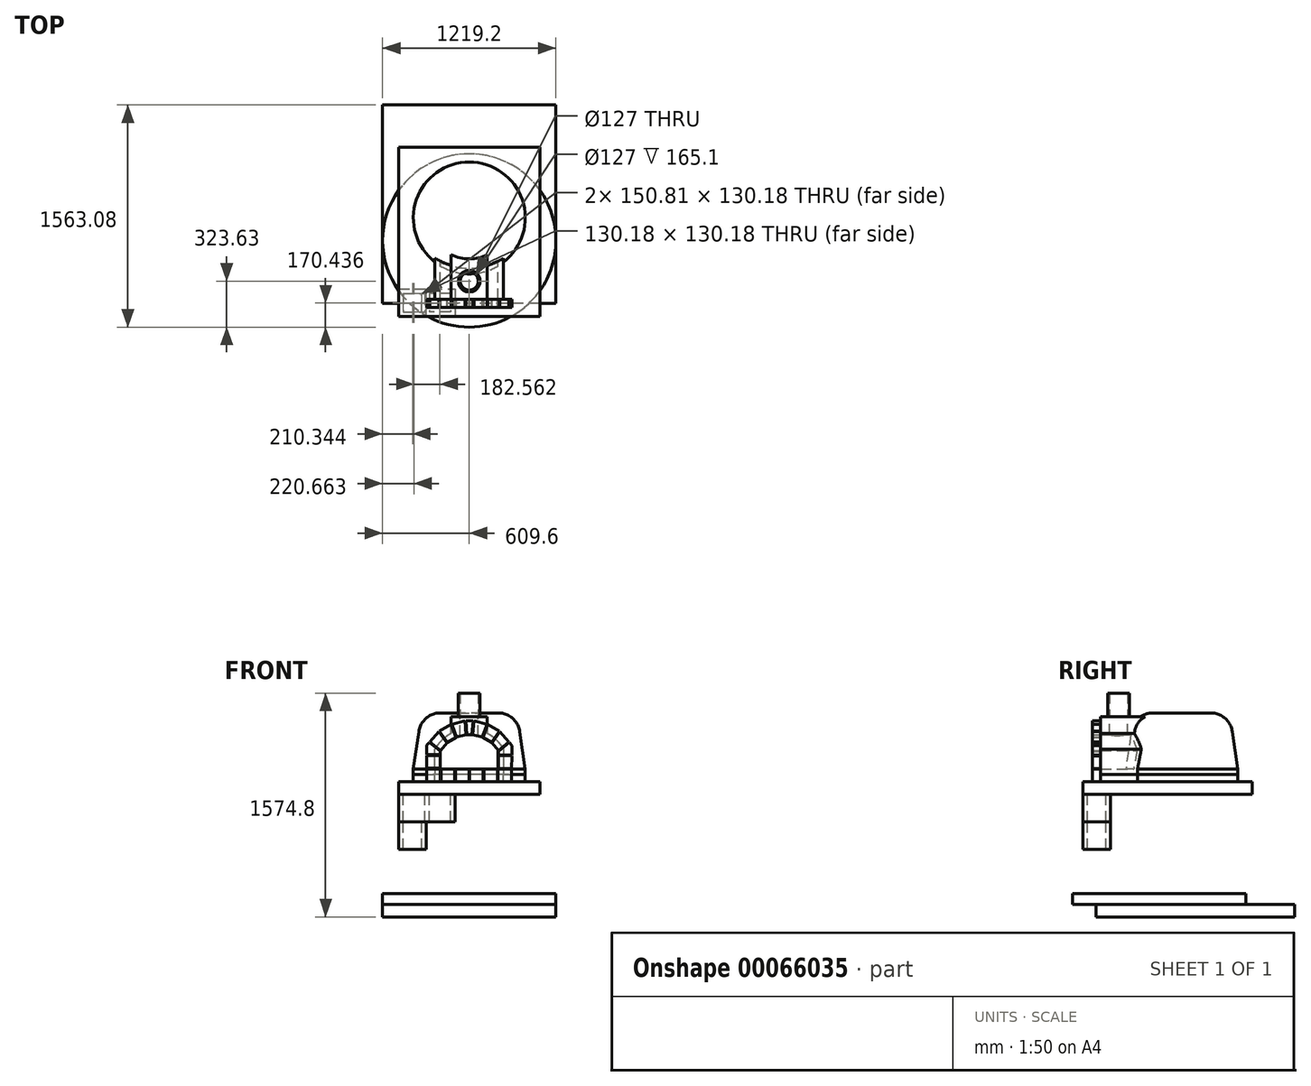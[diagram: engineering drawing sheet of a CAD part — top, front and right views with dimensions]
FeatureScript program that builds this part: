
annotation { "Feature Type Name" : "Feature", "Feature Type Description" : "" }
export const myFeature = defineFeature(function(context is Context, id is Id, definition is map)
    precondition{}
    {
        {
            var Q0;
            Q0=qCreatedBy(makeId("Top.planeOp"),FACE);
            var sketch = newSketch(context, id + "F0", { "sketchPlane" : qUnion([Q0])});
            skCircle(sketch, "E0", {"center": v(0, 0) * mm, "radius": 393.7 * mm});
            skSolve(sketch);
        }
        {
            var Q0;
            Q0=makeQuery(id+"F0.imprint","IMPRINT",FACE,{"disambiguationData":[TD([[makeQuery(id+"F0.imprint","IMPRINT",EDGE,{"derivedFrom":sQuery(id+"F0.wireOp",EDGE,"E0")}),1.0]])]});
            extrude(context, id + "F1", {"entities" : qUnion([Q0]), "depth" : 38.1 * mm});
        }
        {
            var Q0;
            Q0=makeQuery(id+"F1.opExtrude","CAP_FACE",FACE,{"disambiguationData":[OSD([sQuery(id+"F0.wireOp",EDGE,"E0")])],"isStart":false});
            extrude(context, id + "F2", {"entities" : qUnion([Q0]), "operationType" : NewBodyOperationType.ADD, "depth" : 393.7 * mm, "hasDraft" : true, "draftAngle" : 8.4 * degree, "draftPullDirection" : true});
        }
        {
            var Q0;
            Q0=makeQuery(id+"F2.opExtrude","CAP_EDGE",EDGE,{"disambiguationData":[OSD([sQuery(id+"F0.wireOp",EDGE,"E0")])],"isStart":false});
            fillet(context, id + "F3", {"entities" : qUnion([Q0]), "radius" : 152.4 * mm, "tangentPropagation" : true, "allowEdgeOverflow" : false});
        }
        {
            var Q0;
            Q0=qCreatedBy(makeId("Front.planeOp"),FACE);
            var sketch = newSketch(context, id + "F4", { "sketchPlane" : qUnion([Q0])});
            skLineSegment(sketch, "E1", {"start": v(0, 0) * mm, "end": v(-241.3, 0) * mm});
            skLineSegment(sketch, "E2", {"start": v(-241.3, 0) * mm, "end": v(-241.3, 177.8) * mm});
            skLineSegment(sketch, "E3", {"start": v(241.3, 177.8) * mm, "end": v(241.3, 0) * mm});
            skLineSegment(sketch, "E4", {"start": v(241.3, 0) * mm, "end": v(0, 0) * mm});
            skLineSegment(sketch, "E5", {"start": v(-203.2, 167.24) * mm, "end": v(-203.2, 38.1) * mm});
            skLineSegment(sketch, "E6", {"start": v(-203.2, 38.1) * mm, "end": v(203.2, 38.1) * mm});
            skLineSegment(sketch, "E7", {"start": v(203.2, 38.1) * mm, "end": v(203.2, 167.24) * mm});
            skLineSegment(sketch, "E8", {"start": v(0, 279.4) * mm, "end": v(0, 38.1) * mm, "construction": true});
            skLineSegment(sketch, "E9", {"start": v(0, 279.4) * mm, "end": v(0, 317.5) * mm, "construction": true});
            skArc(sketch, "E10", {"start": v(241.3, 177.8) * mm, "mid": v(0, 317.5) * mm, "end": v(-241.3, 177.8) * mm});
            skArc(sketch, "E11.0", {"start": v(203.2, 167.24) * mm, "mid": v(0, 279.4) * mm, "end": v(-203.2, 167.24) * mm});
            skSolve(sketch);
        }
        {
            var Q0;
            Q0 = qSketchRegion(id + "F4", true);
            extrude(context, id + "F5", {"entities" : qUnion([Q0]), "operationType" : NewBodyOperationType.ADD, "depth" : 571.5 * mm});
        }
        {
            var Q0;
            Q0=makeQuery(id+"F5.opExtrude","CAP_FACE",FACE,{"disambiguationData":[OSD([sQuery(id+"F4.wireOp",EDGE,"E1"),sQuery(id+"F4.wireOp",EDGE,"E2"),sQuery(id+"F4.wireOp",EDGE,"E3"),sQuery(id+"F4.wireOp",EDGE,"E4"),sQuery(id+"F4.wireOp",EDGE,"12a89784-33c5-42e5-a8f3-46ffcfec6846"),sQuery(id+"F4.wireOp",EDGE,"6c7c6252-bcdf-4629-810e-ab4d8ebfa29d.0"),sQuery(id+"F4.wireOp",EDGE,"Gnud8bc5-uh5z-W3xU-uaeR-RgDmJmBSCtFp")])],"isStart":false});
            var sketch = newSketch(context, id + "F6", { "sketchPlane" : qUnion([Q0])});
            skLineSegment(sketch, "E12", {"start": v(0, 406.4) * mm, "end": v(-127, 406.4) * mm});
            skPoint(sketch, "E12.startSnap0", {"position": v(0, 304.48) * mm});
            skLineSegment(sketch, "E13", {"start": v(-127, 406.4) * mm, "end": v(-127, 272.25) * mm});
            skLineSegment(sketch, "E14", {"start": v(0, 406.4) * mm, "end": v(127, 406.4) * mm});
            skLineSegment(sketch, "E15", {"start": v(127, 406.4) * mm, "end": v(127, 272.25) * mm});
            skArc(sketch, "E16", {"start": v(127, 272.25) * mm, "mid": v(0, 304.48) * mm, "end": v(-127, 272.25) * mm});
            skSolve(sketch);
        }
        {
            var Q0;
            Q0 = qSketchRegion(id + "F6", true);
            var Q1;
            Q1=makeQuery(id+"F3.opFillet","BLEND_FACE",FACE,{"disambiguationData":[OSD([sQuery(id+"F0.wireOp",EDGE,"E0")])]});
            extrude(context, id + "F7", {"entities" : qUnion([Q0]), "operationType" : NewBodyOperationType.ADD, "endBound" : BoundingType.UP_TO_SURFACE, "oppositeDirection" : true, "endBoundEntityFace" : qUnion([Q1]), "depth" : 355.6 * mm});
        }
        {
            var Q0;
            Q0=makeQuery(id+"F7.opExtrude","SWEPT_FACE",FACE,{"disambiguationData":[OSD([sQuery(id+"F6.wireOp",EDGE,"E12"),sQuery(id+"F6.wireOp",EDGE,"E14")])]});
            var sketch = newSketch(context, id + "F8", { "sketchPlane" : qUnion([Q0])});
            skCircle(sketch, "E17", {"center": v(0, -444.5) * mm, "radius": 63.5 * mm});
            skPoint(sketch, "E17.centerSnap0", {"position": v(0, -571.5) * mm});
            skSolve(sketch);
        }
        {
            var Q0;
            Q0 = qSketchRegion(id + "F8", true);
            extrude(context, id + "F9", {"entities" : qUnion([Q0]), "operationType" : NewBodyOperationType.REMOVE, "oppositeDirection" : true, "depth" : 233.38 * mm});
        }
        {
            var Q0;
            Q0=makeQuery(id+"F5.boolean.opBoolean","MERGE",FACE,{"derivedFrom":[makeQuery(id+"F1.opExtrude","CAP_FACE",FACE,{"disambiguationData":[OSD([sQuery(id+"F0.wireOp",EDGE,"E0")])],"isStart":true}),makeQuery(id+"F5.opExtrude","SWEPT_FACE",FACE,{"disambiguationData":[OSD([sQuery(id+"F4.wireOp",EDGE,"E1"),sQuery(id+"F4.wireOp",EDGE,"E4")])]})]});
            extrude(context, id + "F10", {"entities" : qUnion([Q0]), "depth" : 50.8 * mm});
        }
        {
            var Q0;
            Q0=makeQuery(id+"F7.opExtrude","SWEPT_FACE",FACE,{"disambiguationData":[OSD([sQuery(id+"F6.wireOp",EDGE,"E12"),sQuery(id+"F6.wireOp",EDGE,"E14")])]});
            var sketch = newSketch(context, id + "F11", { "sketchPlane" : qUnion([Q0])});
            skCircle(sketch, "E18", {"center": v(0, -444.5) * mm, "radius": 63.5 * mm});
            skCircle(sketch, "E19", {"center": v(0, -444.5) * mm, "radius": 76.2 * mm});
            skSolve(sketch);
        }
        {
            var Q0;
            Q0 = qSketchRegion(id + "F11", true);
            extrude(context, id + "F12", {"entities" : qUnion([Q0]), "depth" : 165.1 * mm});
        }
        {
            var Q0;
            Q0=makeQuery(id+"F10.opExtrude","CAP_FACE",FACE,{"disambiguationData":[OSD([sQuery(id+"F0.wireOp",EDGE,"E0"),sQuery(id+"F4.wireOp",EDGE,"E1"),sQuery(id+"F4.wireOp",EDGE,"E4")])],"isStart":false});
            cPlane(context, id + "F13", {"entities" : qUnion([Q0]), "cplaneType" : CPlaneType.OFFSET, "offset" : 0 * mm, "width" : 152.4 * mm, "height" : 152.4 * mm});
        }
        {
            var Q0;
            Q0=qCreatedBy(id+"F13.planeOp",FACE);
            cPlane(context, id + "F14", {"entities" : qUnion([Q0]), "cplaneType" : CPlaneType.OFFSET, "offset" : 88.9 * mm, "width" : 152.4 * mm, "height" : 152.4 * mm});
        }
        {
            var Q0;
            Q0=qCreatedBy(makeId("Top.planeOp"),FACE);
            cPlane(context, id + "F15", {"entities" : qUnion([Q0]), "cplaneType" : CPlaneType.OFFSET, "offset" : 914.4 * mm, "oppositeDirection" : true, "width" : 152.4 * mm, "height" : 152.4 * mm});
        }
        {
            var Q0;
            Q0=makeQuery(id+"F10.opExtrude","SWEPT_FACE",FACE,{"disambiguationData":[OSD([sQuery(id+"F4.wireOp",EDGE,"E1"),sQuery(id+"F4.wireOp",EDGE,"E4")])]});
            var sketch = newSketch(context, id + "F16", { "sketchPlane" : qUnion([Q0])});
            skLineSegment(sketch, "E20.bottom", {"start": v(-203.2, 43.18) * mm, "end": v(-298.45, 43.18) * mm});
            skLineSegment(sketch, "E20.top", {"start": v(-203.2, 132.08) * mm, "end": v(-298.45, 132.08) * mm});
            skLineSegment(sketch, "E20.left", {"start": v(-203.2, 43.18) * mm, "end": v(-203.2, 132.08) * mm});
            skLineSegment(sketch, "E20.right", {"start": v(-298.45, 43.18) * mm, "end": v(-298.45, 132.08) * mm});
            skLineSegment(sketch, "E21.bottom", {"start": v(-203.2, 137.16) * mm, "end": v(-298.45, 137.16) * mm});
            skLineSegment(sketch, "E21.top", {"start": v(-203.2, 162.56) * mm, "end": v(-279.93, 224.7) * mm});
            skLineSegment(sketch, "E21.left", {"start": v(-203.2, 137.16) * mm, "end": v(-203.2, 162.56) * mm});
            skLineSegment(sketch, "E21.right", {"start": v(-298.45, 137.16) * mm, "end": v(-298.45, 205.22) * mm});
            skLineSegment(sketch, "E22.bottom", {"start": v(-203.2, 38.1) * mm, "end": v(-298.45, 38.1) * mm});
            skLineSegment(sketch, "E22.top", {"start": v(-203.2, -50.8) * mm, "end": v(-298.45, -50.8) * mm});
            skLineSegment(sketch, "E22.left", {"start": v(-203.2, 38.1) * mm, "end": v(-203.2, -50.8) * mm});
            skLineSegment(sketch, "E22.right", {"start": v(-298.45, 38.1) * mm, "end": v(-298.45, -50.8) * mm});
            skLineSegment(sketch, "E23.bottom", {"start": v(-198.12, 38.1) * mm, "end": v(-102.87, 38.1) * mm});
            skLineSegment(sketch, "E23.top", {"start": v(-198.12, -50.8) * mm, "end": v(-102.87, -50.8) * mm});
            skLineSegment(sketch, "E23.left", {"start": v(-198.12, 38.1) * mm, "end": v(-198.12, -50.8) * mm});
            skLineSegment(sketch, "E23.right", {"start": v(-102.87, 38.1) * mm, "end": v(-102.87, -50.8) * mm});
            skLineSegment(sketch, "E24.bottom", {"start": v(-97.8, 38.01) * mm, "end": v(-2.54, 38.01) * mm});
            skLineSegment(sketch, "E24.top", {"start": v(-97.79, -50.8) * mm, "end": v(-2.54, -50.8) * mm});
            skLineSegment(sketch, "E24.left", {"start": v(-97.8, 38.01) * mm, "end": v(-97.79, -50.8) * mm});
            skLineSegment(sketch, "E24.right", {"start": v(-2.54, 38.01) * mm, "end": v(-2.54, -50.8) * mm});
            skLineSegment(sketch, "E25.bottom", {"start": v(2.54, -50.8) * mm, "end": v(97.8, -50.8) * mm});
            skLineSegment(sketch, "E25.top", {"start": v(2.54, 38.01) * mm, "end": v(97.8, 38.01) * mm});
            skLineSegment(sketch, "E25.left", {"start": v(2.54, -50.8) * mm, "end": v(2.54, 38.01) * mm});
            skLineSegment(sketch, "E25.right", {"start": v(97.8, -50.8) * mm, "end": v(97.8, 38.01) * mm});
            skLineSegment(sketch, "E26.bottom", {"start": v(203.2, 38.01) * mm, "end": v(298.45, 38.01) * mm});
            skLineSegment(sketch, "E26.top", {"start": v(203.2, -50.8) * mm, "end": v(298.45, -50.8) * mm});
            skLineSegment(sketch, "E26.left", {"start": v(203.2, 38.01) * mm, "end": v(203.2, -50.8) * mm});
            skLineSegment(sketch, "E26.right", {"start": v(298.45, 38.01) * mm, "end": v(298.45, -50.8) * mm});
            skLineSegment(sketch, "E27.bottom", {"start": v(102.87, -50.8) * mm, "end": v(198.12, -50.8) * mm});
            skLineSegment(sketch, "E27.top", {"start": v(102.87, 38.01) * mm, "end": v(198.12, 38.01) * mm});
            skLineSegment(sketch, "E27.left", {"start": v(102.87, -50.8) * mm, "end": v(102.87, 38.01) * mm});
            skLineSegment(sketch, "E27.right", {"start": v(198.12, -50.8) * mm, "end": v(198.12, 38.01) * mm});
            skLineSegment(sketch, "E28", {"start": v(-202.54, 168.56) * mm, "end": v(-157.66, 220.6) * mm});
            skLineSegment(sketch, "E29", {"start": v(-157.66, 220.6) * mm, "end": v(-214.4, 300.67) * mm});
            skLineSegment(sketch, "E30", {"start": v(-214.4, 300.67) * mm, "end": v(-276.6, 228.53) * mm});
            skLineSegment(sketch, "E31", {"start": v(-276.6, 228.53) * mm, "end": v(-202.54, 168.56) * mm});
            skLineSegment(sketch, "E32", {"start": v(-154.77, 225.31) * mm, "end": v(-210.12, 303.42) * mm});
            skLineSegment(sketch, "E33", {"start": v(-210.12, 303.42) * mm, "end": v(-127.28, 350.43) * mm});
            skLineSegment(sketch, "E34", {"start": v(-127.28, 350.43) * mm, "end": v(-94.03, 259.79) * mm});
            skLineSegment(sketch, "E35", {"start": v(-94.03, 259.79) * mm, "end": v(-154.77, 225.31) * mm});
            skLineSegment(sketch, "E36", {"start": v(0, 0) * mm, "end": v(-315.29, 262.4) * mm, "construction": true});
            skLineSegment(sketch, "E37", {"start": v(0, 0) * mm, "end": v(-296.3, 423.06) * mm, "construction": true});
            skLineSegment(sketch, "E38", {"start": v(0, 0) * mm, "end": v(-160.4, 451.18) * mm, "construction": true});
            skLineSegment(sketch, "E39", {"start": v(-279.93, 224.7) * mm, "end": v(-298.45, 205.22) * mm});
            skLineSegment(sketch, "E40", {"start": v(-30.19, 375.45) * mm, "end": v(-122.63, 352.51) * mm});
            skLineSegment(sketch, "E41", {"start": v(-122.63, 352.51) * mm, "end": v(-89.63, 262.56) * mm});
            skLineSegment(sketch, "E42", {"start": v(0, 0) * mm, "end": v(-30.49, 445.38) * mm, "construction": true});
            skLineSegment(sketch, "E43", {"start": v(0, 0) * mm, "end": v(2.54, 799.68) * mm, "construction": true});
            skLineSegment(sketch, "E44", {"start": v(-30.19, 375.45) * mm, "end": v(-23.03, 279.09) * mm});
            skLineSegment(sketch, "E45", {"start": v(-23.03, 279.09) * mm, "end": v(-89.63, 262.56) * mm});
            skLineSegment(sketch, "E46", {"start": v(0.89, 279.47) * mm, "end": v(-17.47, 279.53) * mm});
            skLineSegment(sketch, "E47", {"start": v(-17.47, 279.53) * mm, "end": v(-23.95, 376.97) * mm});
            skLineSegment(sketch, "E48", {"start": v(-23.95, 376.97) * mm, "end": v(1.2, 376.9) * mm});
            skLineSegment(sketch, "E49.MirrorCS", {"start": v(156.2, 224.33) * mm, "end": v(212.05, 302.08) * mm});
            skLineSegment(sketch, "E50.MirrorCS", {"start": v(278.04, 226.77) * mm, "end": v(203.6, 167.27) * mm});
            skLineSegment(sketch, "E51.MirrorCS", {"start": v(19.25, 279.41) * mm, "end": v(26.34, 376.81) * mm});
            skLineSegment(sketch, "E52.MirrorCS", {"start": v(204.03, 130.79) * mm, "end": v(299.28, 130.18) * mm});
            skLineSegment(sketch, "E53.MirrorCS", {"start": v(32.57, 375.25) * mm, "end": v(24.8, 278.93) * mm});
            skLineSegment(sketch, "E54.MirrorCS", {"start": v(203.47, 41.89) * mm, "end": v(204.03, 130.79) * mm});
            skLineSegment(sketch, "E55.MirrorCS", {"start": v(298.72, 41.28) * mm, "end": v(299.28, 130.18) * mm});
            skLineSegment(sketch, "E56.MirrorCS", {"start": v(216.3, 299.3) * mm, "end": v(278.04, 226.77) * mm});
            skLineSegment(sketch, "E57.MirrorCS", {"start": v(0.89, 279.47) * mm, "end": v(19.25, 279.41) * mm});
            skLineSegment(sketch, "E58.MirrorCS", {"start": v(129.5, 349.62) * mm, "end": v(95.68, 259.18) * mm});
            skLineSegment(sketch, "E59.MirrorCS", {"start": v(32.57, 375.25) * mm, "end": v(124.87, 351.72) * mm});
            skLineSegment(sketch, "E60.MirrorCS", {"start": v(124.87, 351.72) * mm, "end": v(91.3, 261.99) * mm});
            skLineSegment(sketch, "E61.MirrorCS", {"start": v(281.35, 222.91) * mm, "end": v(299.75, 203.32) * mm});
            skLineSegment(sketch, "E62.MirrorCS", {"start": v(204.07, 135.87) * mm, "end": v(204.23, 161.27) * mm});
            skLineSegment(sketch, "E63.MirrorCS", {"start": v(95.68, 259.18) * mm, "end": v(156.2, 224.33) * mm});
            skLineSegment(sketch, "E64.MirrorCS", {"start": v(299.32, 135.26) * mm, "end": v(299.75, 203.32) * mm});
            skLineSegment(sketch, "E65.MirrorCS", {"start": v(204.23, 161.27) * mm, "end": v(281.35, 222.91) * mm});
            skLineSegment(sketch, "E66.MirrorCS", {"start": v(26.34, 376.81) * mm, "end": v(1.2, 376.9) * mm});
            skLineSegment(sketch, "E67.MirrorCS", {"start": v(204.07, 135.87) * mm, "end": v(299.32, 135.26) * mm});
            skLineSegment(sketch, "E68.MirrorCS", {"start": v(203.6, 167.27) * mm, "end": v(159.06, 219.6) * mm});
            skLineSegment(sketch, "E69.MirrorCS", {"start": v(212.05, 302.08) * mm, "end": v(129.5, 349.62) * mm});
            skLineSegment(sketch, "E70.MirrorCS", {"start": v(159.06, 219.6) * mm, "end": v(216.3, 299.3) * mm});
            skLineSegment(sketch, "E71.MirrorCS", {"start": v(203.47, 41.89) * mm, "end": v(298.72, 41.28) * mm});
            skLineSegment(sketch, "E72.MirrorCS", {"start": v(24.8, 278.93) * mm, "end": v(91.3, 261.99) * mm});
            skSolve(sketch);
        }
        {
            var Q0;
            Q0 = qSketchRegion(id + "F16", true);
            extrude(context, id + "F17", {"entities" : qUnion([Q0]), "depth" : 57.15 * mm});
        }
        {
            var Q0;
            Q0=qCreatedBy(id+"F13.planeOp",FACE);
            var sketch = newSketch(context, id + "F18", { "sketchPlane" : qUnion([Q0])});
            skLineSegment(sketch, "E73", {"start": v(-496.1, -496.1) * mm, "end": v(496.1, -496.1) * mm});
            skLineSegment(sketch, "E74", {"start": v(-496.1, -496.1) * mm, "end": v(-496.1, 694.53) * mm});
            skLineSegment(sketch, "E75.0.1.0", {"start": v(-496.1, -297.66) * mm, "end": v(496.1, -297.66) * mm});
            skLineSegment(sketch, "E75.0.2.0", {"start": v(-496.1, -99.22) * mm, "end": v(496.1, -99.22) * mm});
            skLineSegment(sketch, "E75.0.3.0", {"start": v(-496.1, 99.22) * mm, "end": v(496.1, 99.22) * mm});
            skLineSegment(sketch, "E75.0.4.0", {"start": v(-496.1, 297.66) * mm, "end": v(496.1, 297.66) * mm});
            skLineSegment(sketch, "E75.0.5.0", {"start": v(-496.1, 496.1) * mm, "end": v(496.1, 496.1) * mm});
            skLineSegment(sketch, "E75.0.5.1", {"start": v(-496.1, 496.1) * mm, "end": v(-496.1, 694.53) * mm});
            skLineSegment(sketch, "E75.0.6.0", {"start": v(-496.1, 694.53) * mm, "end": v(297.66, 694.53) * mm});
            skLineSegment(sketch, "E75.1.0.1", {"start": v(-297.66, -496.1) * mm, "end": v(-297.66, 694.53) * mm});
            skLineSegment(sketch, "E75.2.0.1", {"start": v(-99.22, -496.1) * mm, "end": v(-99.22, 694.53) * mm});
            skLineSegment(sketch, "E75.3.0.1", {"start": v(99.22, -496.1) * mm, "end": v(99.22, 694.53) * mm});
            skLineSegment(sketch, "E75.4.0.1", {"start": v(297.66, -496.1) * mm, "end": v(297.66, 694.53) * mm});
            skLineSegment(sketch, "E75.5.0.1", {"start": v(496.1, -496.1) * mm, "end": v(496.1, 694.53) * mm});
            skLineSegment(sketch, "E75.direction1", {"start": v(-496.1, -496.1) * mm, "end": v(-297.66, -496.1) * mm, "construction": true});
            skLineSegment(sketch, "E75.direction2", {"start": v(-496.1, -496.1) * mm, "end": v(-496.1, -297.66) * mm, "construction": true});
            skLineSegment(sketch, "E76", {"start": v(297.66, 694.53) * mm, "end": v(496.1, 694.53) * mm});
            skLineSegment(sketch, "E77", {"start": v(0, -496.1) * mm, "end": v(0, -297.66) * mm, "construction": true});
            skLineSegment(sketch, "E78.trimOffspring", {"start": v(0, 297.66) * mm, "end": v(0, 694.53) * mm, "construction": true});
            skLineSegment(sketch, "E79.trimOffspring", {"start": v(0, -99.22) * mm, "end": v(0, 99.22) * mm, "construction": true});
            skLineSegment(sketch, "E80", {"start": v(0, 0) * mm, "end": v(99.22, 0) * mm, "construction": true});
            skSolve(sketch);
        }
        {
            var Q0;
            Q0=qCreatedBy(id+"F15.planeOp",FACE);
            var sketch = newSketch(context, id + "F19", { "sketchPlane" : qUnion([Q0])});
            skLineSegment(sketch, "E81.rect.bottom", {"start": v(609.6, 794.95) * mm, "end": v(-609.6, 794.95) * mm});
            skLineSegment(sketch, "E81.rect.top", {"start": v(609.6, -602.05) * mm, "end": v(-609.6, -602.05) * mm});
            skLineSegment(sketch, "E81.rect.left", {"start": v(609.6, 794.95) * mm, "end": v(609.6, -602.05) * mm});
            skLineSegment(sketch, "E81.rect.right", {"start": v(-609.6, 794.95) * mm, "end": v(-609.6, -602.05) * mm});
            skPoint(sketch, "E81.rect.middle", {"position": v(0, 96.45) * mm});
            skSolve(sketch);
        }
        {
            var Q0;
            Q0=qCreatedBy(id+"F14.planeOp",FACE);
            var sketch = newSketch(context, id + "F20", { "sketchPlane" : qUnion([Q0])});
            skLineSegment(sketch, "E82.0", {"start": v(-496.1, 496.1) * mm, "end": v(-496.1, 694.53) * mm});
            skLineSegment(sketch, "E82.1", {"start": v(-496.1, 694.53) * mm, "end": v(-99.22, 694.53) * mm});
            skLineSegment(sketch, "E82.2", {"start": v(-99.22, 500.86) * mm, "end": v(-99.22, 694.53) * mm});
            skLineSegment(sketch, "E82.3", {"start": v(-496.1, 500.86) * mm, "end": v(-99.22, 500.86) * mm});
            skPoint(sketch, "E83.orphan", {"position": v(-99.22, -496.1) * mm});
            skPoint(sketch, "E84.orphan", {"position": v(297.66, 694.53) * mm});
            skLineSegment(sketch, "E85.bottom", {"start": v(-464.34, 532.6) * mm, "end": v(-313.53, 532.6) * mm});
            skLineSegment(sketch, "E85.top", {"start": v(-464.34, 662.78) * mm, "end": v(-313.53, 662.78) * mm});
            skLineSegment(sketch, "E85.left", {"start": v(-464.34, 532.6) * mm, "end": v(-464.34, 662.78) * mm});
            skLineSegment(sketch, "E85.right", {"start": v(-313.53, 532.6) * mm, "end": v(-313.53, 662.78) * mm});
            skLineSegment(sketch, "E86.bottom", {"start": v(-130.97, 532.6) * mm, "end": v(-281.78, 532.6) * mm});
            skLineSegment(sketch, "E86.top", {"start": v(-130.97, 662.78) * mm, "end": v(-281.78, 662.78) * mm});
            skLineSegment(sketch, "E86.left", {"start": v(-130.97, 532.6) * mm, "end": v(-130.97, 662.78) * mm});
            skLineSegment(sketch, "E86.right", {"start": v(-281.78, 532.6) * mm, "end": v(-281.78, 662.78) * mm});
            skSolve(sketch);
        }
        {
            var Q0;
            Q0 = qSketchRegion(id + "F20", true);
            extrude(context, id + "F21", {"entities" : qUnion([Q0]), "depth" : 193.67 * mm});
        }
        {
            var Q0;
            Q0=qCreatedBy(id+"F13.planeOp",FACE);
            var sketch = newSketch(context, id + "F22", { "sketchPlane" : qUnion([Q0])});
            skLineSegment(sketch, "E87.0", {"start": v(-496.1, -496.1) * mm, "end": v(496.1, -496.1) * mm});
            skLineSegment(sketch, "E87.1", {"start": v(-496.1, -496.1) * mm, "end": v(-496.1, 694.53) * mm});
            skLineSegment(sketch, "E87.2", {"start": v(-496.1, 694.53) * mm, "end": v(297.66, 694.53) * mm});
            skLineSegment(sketch, "E87.3", {"start": v(297.66, 694.53) * mm, "end": v(496.1, 694.53) * mm});
            skLineSegment(sketch, "E87.4", {"start": v(496.1, -496.1) * mm, "end": v(496.1, 694.53) * mm});
            skSolve(sketch);
        }
        {
            var Q0;
            Q0 = qSketchRegion(id + "F22", true);
            extrude(context, id + "F23", {"entities" : qUnion([Q0]), "depth" : 88.9 * mm});
        }
        {
            var Q0;
            Q0=makeQuery(id+"F21.opExtrude","CAP_FACE",FACE,{"disambiguationData":[OSD([sQuery(id+"F20.wireOp",EDGE,"E82.0"),sQuery(id+"F20.wireOp",EDGE,"E82.1"),sQuery(id+"F20.wireOp",EDGE,"E82.2"),sQuery(id+"F20.wireOp",EDGE,"E82.3"),sQuery(id+"F20.wireOp",EDGE,"E85.bottom"),sQuery(id+"F20.wireOp",EDGE,"E85.top"),sQuery(id+"F20.wireOp",EDGE,"E85.left"),sQuery(id+"F20.wireOp",EDGE,"E85.right"),sQuery(id+"F20.wireOp",EDGE,"E86.bottom"),sQuery(id+"F20.wireOp",EDGE,"E86.top"),sQuery(id+"F20.wireOp",EDGE,"E86.left"),sQuery(id+"F20.wireOp",EDGE,"E86.right")])],"isStart":false});
            var sketch = newSketch(context, id + "F24", { "sketchPlane" : qUnion([Q0])});
            skLineSegment(sketch, "E88.0.0", {"start": v(-496.1, 694.53) * mm, "end": v(-496.1, 500.86) * mm});
            skLineSegment(sketch, "E88.0.1", {"start": v(-496.1, 500.86) * mm, "end": v(-302.42, 500.86) * mm});
            skLineSegment(sketch, "E88.0.3", {"start": v(-302.42, 694.53) * mm, "end": v(-496.1, 694.53) * mm});
            skLineSegment(sketch, "E89", {"start": v(-302.42, 694.53) * mm, "end": v(-302.42, 500.86) * mm});
            skLineSegment(sketch, "E90.0", {"start": v(-334.17, 662.78) * mm, "end": v(-334.17, 532.6) * mm});
            skLineSegment(sketch, "E90.1", {"start": v(-334.17, 662.78) * mm, "end": v(-464.34, 662.78) * mm});
            skLineSegment(sketch, "E90.2", {"start": v(-464.34, 662.78) * mm, "end": v(-464.34, 532.6) * mm});
            skLineSegment(sketch, "E90.3", {"start": v(-464.34, 532.6) * mm, "end": v(-334.17, 532.6) * mm});
            skSolve(sketch);
        }
        {
            var Q0;
            Q0 = qSketchRegion(id + "F24", true);
            extrude(context, id + "F25", {"entities" : qUnion([Q0]), "depth" : 193.67 * mm});
        }
        {
            var Q0;
            Q0 = qSketchRegion(id + "F19", true);
            extrude(context, id + "F26", {"entities" : qUnion([Q0]), "oppositeDirection" : true, "depth" : 88.9 * mm});
        }
        {
            var Q0;
            Q0=qCreatedBy(id+"F15.planeOp",FACE);
            var sketch = newSketch(context, id + "F27", { "sketchPlane" : qUnion([Q0])});
            skCircle(sketch, "E91", {"center": v(0, -158.53) * mm, "radius": 609.6 * mm});
            skSolve(sketch);
        }
        {
            var Q0;
            Q0 = qSketchRegion(id + "F27", true);
            extrude(context, id + "F28", {"entities" : qUnion([Q0]), "depth" : 76.2 * mm});
        }
    });
